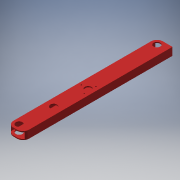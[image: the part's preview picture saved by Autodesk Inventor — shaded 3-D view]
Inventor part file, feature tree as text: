
AUTODESK INVENTOR PART (.ipt)
format: ipt  version: 2017 SP1 (Build 210196100, 196)  size: 159,232 bytes
history: native  units: in
note: dims shown in document units (in); Inventor stores cm internally (conversion verified against a paired STEP export)
features: extrude x2, sketch x2, fillet x1
ambient origin geometry x8: Origin, YZ Plane, XZ Plane, XY Plane, X Axis, Y Axis, Z Axis, Center Point
bodies: Solid1 (feature_tree)
feature tree (5):
  extrude  "Extrusion1"  Depth=2.0in
  extrude  "Extrusion2"  Depth=19.25in TaperAngle=0.0deg
  fillet  "Fillet1"  Radius=0.875in
  sketch  "Sketch1"  dims[d0=1.0in d1=2.0in]
  sketch  "Sketch2"  dims[d2=0.125in d3=19.25in d4=0.0in d5=0.875in d10=0.875in d11=20.0in d12=0.0in d13=0.75in d16=0.75in d17=0.75in d20=0.75in d21=0.625in d23=0.75in d24=1.5in d27=1.125in d28=0.15in d29=0.875in d31=4.201in d32=1.125in d34=0.25in]
